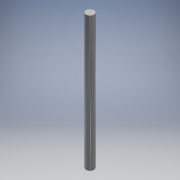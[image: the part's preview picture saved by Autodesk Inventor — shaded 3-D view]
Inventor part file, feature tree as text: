
AUTODESK INVENTOR PART (.ipt)
format: ipt  version: 2017 (Build 210142000, 142)  size: 92,672 bytes
history: native  units: in
note: dims shown in document units (in); Inventor stores cm internally (conversion verified against a paired STEP export)
features: extrude x1, sketch x1
ambient origin geometry x8: Origin, YZ Plane, XZ Plane, XY Plane, X Axis, Y Axis, Z Axis, Center Point
bodies: Solid1 (feature_tree)
feature tree (2):
  extrude  "Extrusion1"  [1 undecoded]
  sketch  "Sketch1"  dims[d1=2.0in d2=0.0in]
note: 1 required parameter value undecoded (feature->parameter linkage not recoverable at this tier; creation-order binding heuristic only, values carry confidence <= 0.55)
